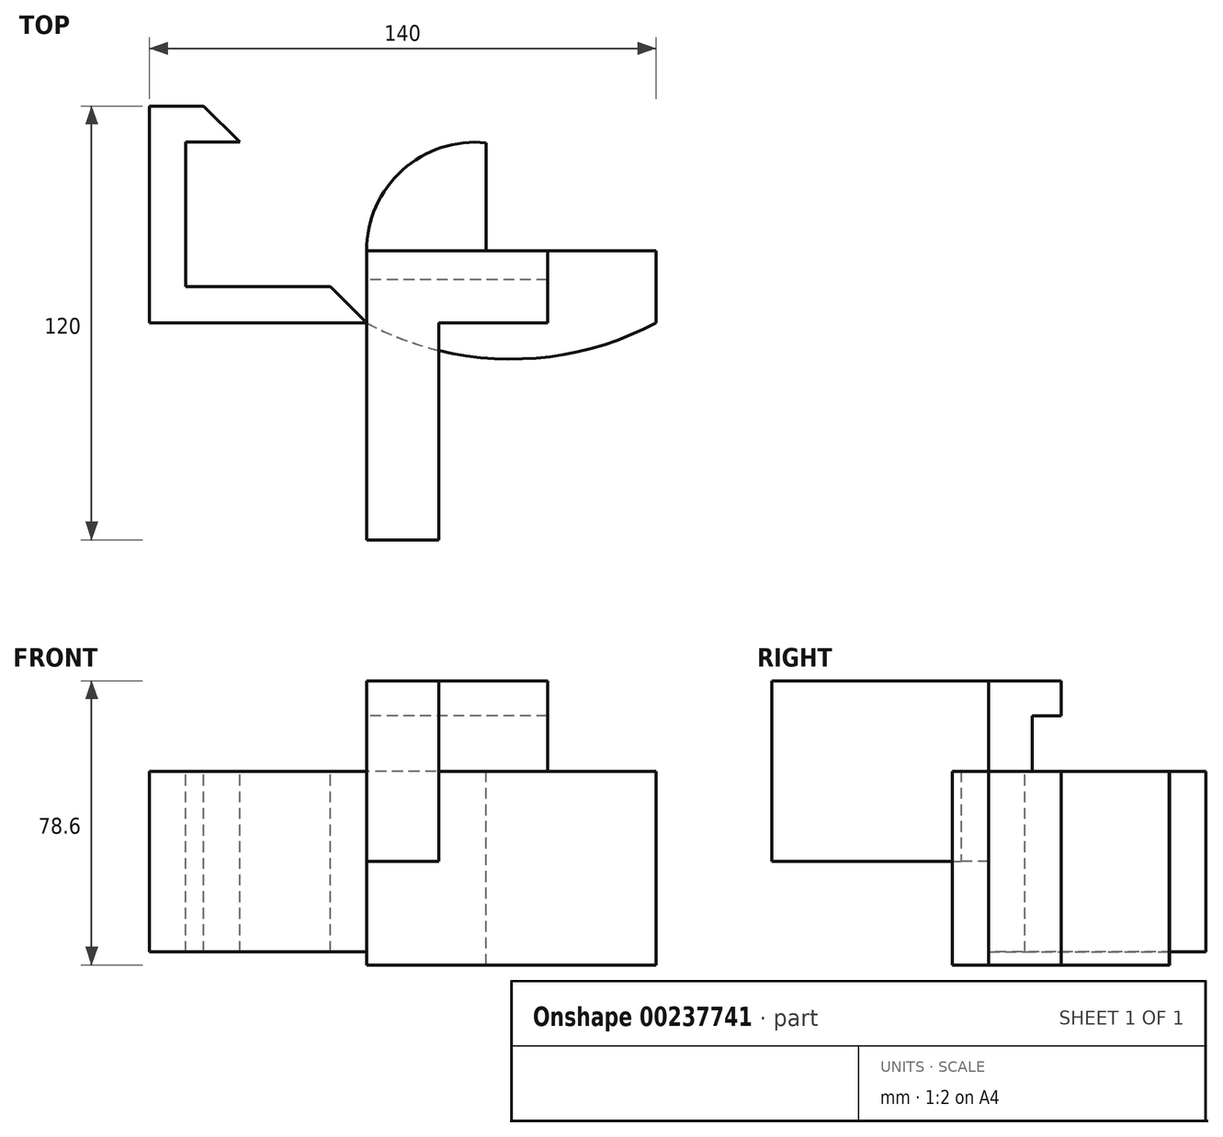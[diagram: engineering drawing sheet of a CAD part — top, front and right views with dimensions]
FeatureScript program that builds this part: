
annotation { "Feature Type Name" : "Feature", "Feature Type Description" : "" }
export const myFeature = defineFeature(function(context is Context, id is Id, definition is map)
    precondition{}
    {
        {
            var Q0;
            Q0=qCreatedBy(makeId("Top.planeOp"),FACE);
            var sketch = newSketch(context, id + "F0", { "sketchPlane" : qUnion([Q0])});
            skLineSegment(sketch, "E0", {"start": v(-45, 60) * mm, "end": v(-60, 60) * mm});
            skLineSegment(sketch, "E1", {"start": v(-60, 60) * mm, "end": v(-60, 0) * mm});
            skLineSegment(sketch, "E2", {"start": v(-60, 0) * mm, "end": v(0, 0) * mm});
            skLineSegment(sketch, "E3", {"start": v(0, 0) * mm, "end": v(-10, 10) * mm});
            skLineSegment(sketch, "E4", {"start": v(-10, 10) * mm, "end": v(-50, 10) * mm});
            skLineSegment(sketch, "E5", {"start": v(-50, 10) * mm, "end": v(-50, 50) * mm});
            skLineSegment(sketch, "E6", {"start": v(-50, 50) * mm, "end": v(-35, 50) * mm});
            skLineSegment(sketch, "E7", {"start": v(-35, 50) * mm, "end": v(-45, 60) * mm});
            skSolve(sketch);
        }
        {
            var Q0;
            Q0=qCreatedBy(makeId("Top.planeOp"),FACE);
            var sketch = newSketch(context, id + "F1", { "sketchPlane" : qUnion([Q0])});
            skLineSegment(sketch, "E8", {"start": v(33.03, 49.85) * mm, "end": v(33.03, 20) * mm});
            skLineSegment(sketch, "E9", {"start": v(33.03, 20) * mm, "end": v(80, 20) * mm});
            skLineSegment(sketch, "E10", {"start": v(80, 20) * mm, "end": v(80, 0) * mm});
            skArc(sketch, "E11", {"start": v(33.03, 49.85) * mm, "mid": v(9.89, 42.26) * mm, "end": v(0, 20) * mm});
            skArc(sketch, "E12", {"start": v(0, 0) * mm, "mid": v(40, -10) * mm, "end": v(80, 0) * mm});
            skLineSegment(sketch, "E13", {"start": v(0, 20) * mm, "end": v(0, 0) * mm});
            skSolve(sketch);
        }
        {
            var Q0;
            Q0=makeQuery(id+"F1.imprint","IMPRINT",FACE,{"disambiguationData":[TD([[makeQuery(id+"F1.imprint","IMPRINT",EDGE,{"derivedFrom":sQuery(id+"F1.wireOp",EDGE,"E8")}),-1.0]])]});
            extrude(context, id + "F2", {"entities" : qUnion([Q0]), "oppositeDirection" : true, "depth" : 28.6 * mm});
        }
        {
            var Q0;
            Q0=makeQuery(id+"F0.imprint","IMPRINT",FACE,{"disambiguationData":[TD([[makeQuery(id+"F0.imprint","IMPRINT",EDGE,{"derivedFrom":sQuery(id+"F0.wireOp",EDGE,"E0")}),1.0]])]});
            extrude(context, id + "F3", {"entities" : qUnion([Q0]), "oppositeDirection" : true, "depth" : 25 * mm});
        }
        {
            var Q0;
            Q0=makeQuery(id+"F3.opExtrude","CAP_FACE",FACE,{"disambiguationData":[OSD([sQuery(id+"F0.wireOp",EDGE,"E0"),sQuery(id+"F0.wireOp",EDGE,"E1"),sQuery(id+"F0.wireOp",EDGE,"E2"),sQuery(id+"F0.wireOp",EDGE,"E3"),sQuery(id+"F0.wireOp",EDGE,"E4"),sQuery(id+"F0.wireOp",EDGE,"E5"),sQuery(id+"F0.wireOp",EDGE,"E6"),sQuery(id+"F0.wireOp",EDGE,"E7")])],"isStart":true});
            var Q1;
            Q1=makeQuery(id+"F2.opExtrude","CAP_FACE",FACE,{"disambiguationData":[OSD([sQuery(id+"F1.wireOp",EDGE,"E8"),sQuery(id+"F1.wireOp",EDGE,"E9"),sQuery(id+"F1.wireOp",EDGE,"E10"),sQuery(id+"F1.wireOp",EDGE,"E11"),sQuery(id+"F1.wireOp",EDGE,"E12"),sQuery(id+"F1.wireOp",EDGE,"E13")])],"isStart":true});
            extrude(context, id + "F4", {"entities" : qUnion([Q0, Q1]), "depth" : 25 * mm});
        }
        {
            var Q0;
            Q0=qCreatedBy(makeId("Right.planeOp"),FACE);
            var sketch = newSketch(context, id + "F5", { "sketchPlane" : qUnion([Q0])});
            skLineSegment(sketch, "E14.bottom", {"start": v(-60, 50) * mm, "end": v(0, 50) * mm});
            skLineSegment(sketch, "E14.top", {"start": v(-60, 0) * mm, "end": v(0, 0) * mm});
            skLineSegment(sketch, "E14.left", {"start": v(-60, 50) * mm, "end": v(-60, 0) * mm});
            skLineSegment(sketch, "E14.right", {"start": v(0, 50) * mm, "end": v(0, 0) * mm});
            skLineSegment(sketch, "E15.bottom", {"start": v(0, 50) * mm, "end": v(20, 50) * mm});
            skLineSegment(sketch, "E15.top", {"start": v(0, 0) * mm, "end": v(20, 0) * mm});
            skLineSegment(sketch, "E15.right", {"start": v(20, 50) * mm, "end": v(20, 0) * mm});
            skLineSegment(sketch, "E16.bottom", {"start": v(20, 40.33) * mm, "end": v(12, 40.33) * mm});
            skLineSegment(sketch, "E16.top", {"start": v(20, 10.33) * mm, "end": v(12, 10.33) * mm});
            skLineSegment(sketch, "E16.left", {"start": v(20, 40.33) * mm, "end": v(20, 10.33) * mm});
            skLineSegment(sketch, "E16.right", {"start": v(12, 40.33) * mm, "end": v(12, 10.33) * mm});
            skSolve(sketch);
        }
        {
            var Q0;
            Q0=makeQuery(id+"F5.imprint","IMPRINT",FACE,{"disambiguationData":[TD([[makeQuery(id+"F5.imprint","IMPRINT",EDGE,{"derivedFrom":sQuery(id+"F5.wireOp",EDGE,"E14.bottom")}),-1.0]])]});
            extrude(context, id + "F6", {"entities" : qUnion([Q0]), "depth" : 20 * mm});
        }
        {
            var Q0;
            {var subQ1=sQuery(id+"F5.wireOp",EDGE,"E15.bottom");Q0=makeQuery(id+"F5.imprint","IMPRINT",FACE,{"disambiguationData":[TD([[makeQuery(id+"F5.imprint","IMPRINT",EDGE,{"derivedFrom":subQ1}),-1.0]])]});}
            extrude(context, id + "F7", {"entities" : qUnion([Q0]), "operationType" : NewBodyOperationType.ADD, "depth" : 50 * mm});
        }
    });
